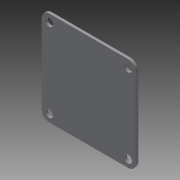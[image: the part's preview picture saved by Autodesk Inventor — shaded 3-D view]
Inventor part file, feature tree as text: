
AUTODESK INVENTOR PART (.ipt)
format: ipt  version: 2015 (Build 190159000, 159)  size: 93,184 bytes
history: native  units: in
note: dims shown in document units (in); Inventor stores cm internally (conversion verified against a paired STEP export)
features: sketch x2, extrude x1, hole x1
ambient origin geometry x8: Origin, YZ Plane, XZ Plane, XY Plane, X Axis, Y Axis, Z Axis, Center Point
bodies: Solid1 (feature_tree)
feature tree (4):
  extrude  "Extrusion1"  Depth=1.4567in
  hole  "Hole1"  [1 undecoded]
  sketch  "Sketch1"  dims[d0=1.4567in d1=1.4567in]
  sketch  "Sketch2"  dims[d2=0.1181in d3=0.0394in d4=0.0in d5=0.1181in d6=0.1181in d7=0.1181in d8=0.1181in d9=0.2362in d10=0.1575in d11=0.0787in d12=90.0deg d13=0.315in d14=0.8108in]
note: 1 required parameter value undecoded (feature->parameter linkage not recoverable at this tier; creation-order binding heuristic only, values carry confidence <= 0.55)
